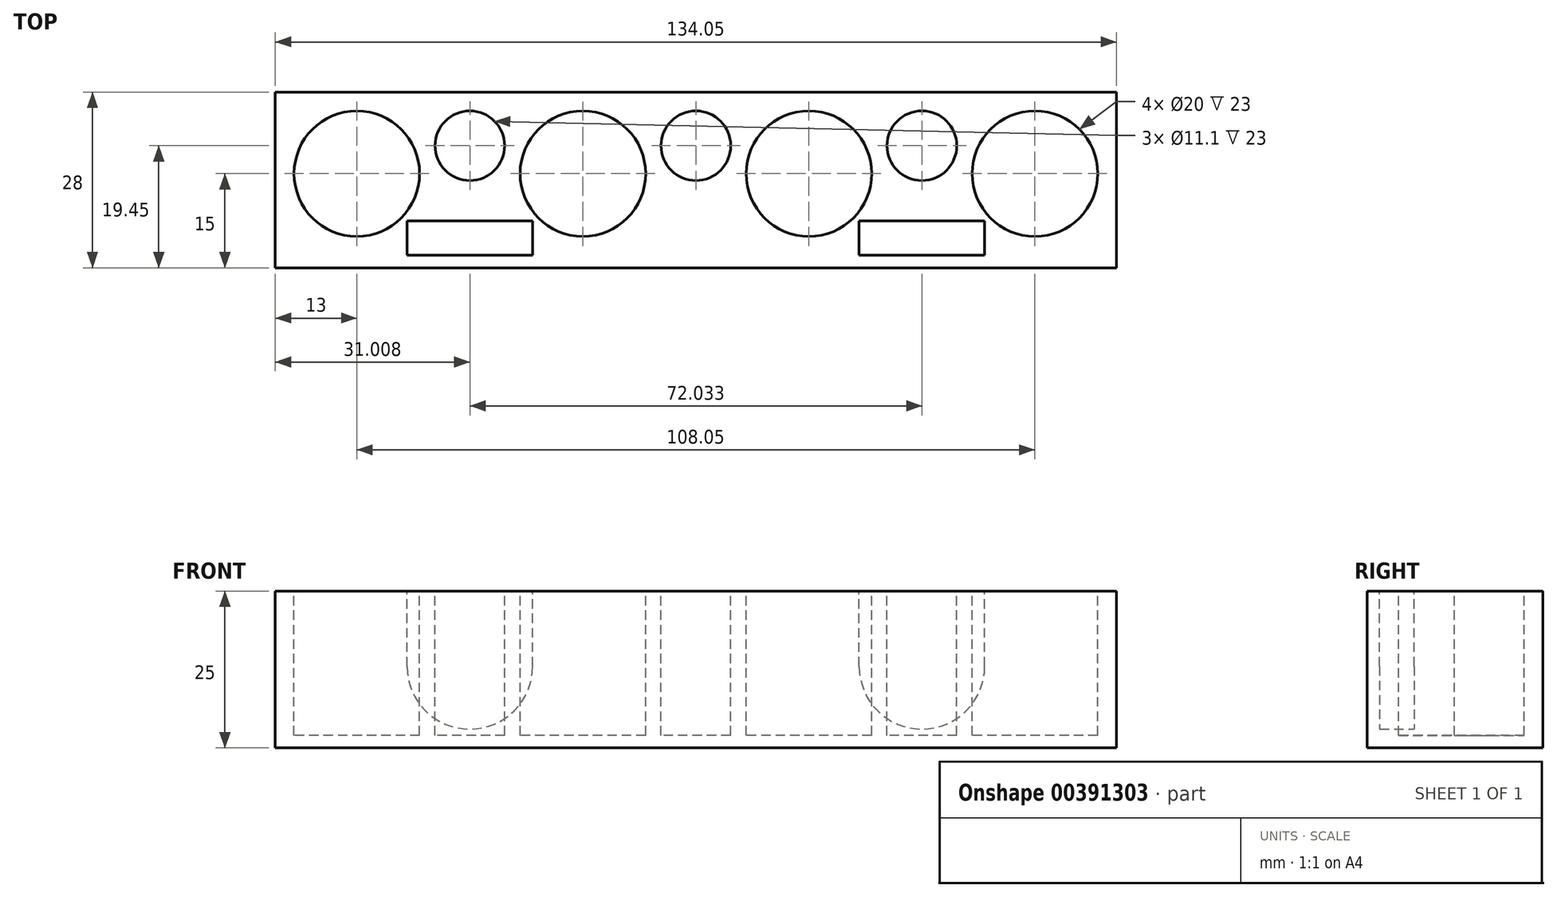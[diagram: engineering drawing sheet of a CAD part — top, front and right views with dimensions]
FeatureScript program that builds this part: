
annotation { "Feature Type Name" : "Feature", "Feature Type Description" : "" }
export const myFeature = defineFeature(function(context is Context, id is Id, definition is map)
    precondition{}
    {
        {
            var Q0;
            Q0=qCreatedBy(makeId("Top.planeOp"),FACE);
            var sketch = newSketch(context, id + "F0", { "sketchPlane" : qUnion([Q0])});
            skLineSegment(sketch, "E0.bottom", {"start": v(0, 0) * mm, "end": v(134.05, 0) * mm});
            skLineSegment(sketch, "E0.top", {"start": v(0, -28) * mm, "end": v(134.05, -28) * mm});
            skLineSegment(sketch, "E0.left", {"start": v(0, 0) * mm, "end": v(0, -28) * mm});
            skLineSegment(sketch, "E0.right", {"start": v(134.05, 0) * mm, "end": v(134.05, -28) * mm});
            skCircle(sketch, "E1", {"center": v(13, -13) * mm, "radius": 10 * mm});
            skCircle(sketch, "E2", {"center": v(31, -8.55) * mm, "radius": 5.55 * mm});
            skCircle(sketch, "E3", {"center": v(49.02, -13) * mm, "radius": 10 * mm});
            skCircle(sketch, "E4", {"center": v(67.02, -8.55) * mm, "radius": 5.55 * mm});
            skCircle(sketch, "E5", {"center": v(85.03, -13) * mm, "radius": 10 * mm});
            skCircle(sketch, "E6", {"center": v(103.04, -8.55) * mm, "radius": 5.55 * mm});
            skCircle(sketch, "E7", {"center": v(121.05, -13) * mm, "radius": 10 * mm});
            skLineSegment(sketch, "E8.bottom", {"start": v(21, -26) * mm, "end": v(41, -26) * mm});
            skLineSegment(sketch, "E8.top", {"start": v(21, -21) * mm, "end": v(41, -21) * mm});
            skLineSegment(sketch, "E8.left", {"start": v(21, -26) * mm, "end": v(21, -21) * mm});
            skLineSegment(sketch, "E8.right", {"start": v(41, -26) * mm, "end": v(41, -21) * mm});
            skCircle(sketch, "E9", {"center": v(31, -33.78) * mm, "radius": 17.5 * mm, "construction": true});
            skLineSegment(sketch, "E10", {"start": v(31, -33.78) * mm, "end": v(31, -13.78) * mm, "construction": true});
            skLineSegment(sketch, "E11", {"start": v(21, -23.5) * mm, "end": v(31, -23.5) * mm, "construction": true});
            skLineSegment(sketch, "E12", {"start": v(31, -23.5) * mm, "end": v(41, -23.78) * mm, "construction": true});
            skLineSegment(sketch, "E13.bottom", {"start": v(93.04, -26) * mm, "end": v(113.04, -26) * mm});
            skLineSegment(sketch, "E13.top", {"start": v(93.04, -21) * mm, "end": v(113.04, -21) * mm});
            skLineSegment(sketch, "E13.left", {"start": v(93.04, -26) * mm, "end": v(93.04, -21) * mm});
            skLineSegment(sketch, "E13.right", {"start": v(113.04, -26) * mm, "end": v(113.04, -21) * mm});
            skCircle(sketch, "E14", {"center": v(103.04, -33.78) * mm, "radius": 17.5 * mm, "construction": true});
            skLineSegment(sketch, "E15", {"start": v(103.04, -33.78) * mm, "end": v(103.04, -13.78) * mm, "construction": true});
            skLineSegment(sketch, "E16", {"start": v(103.04, -23.78) * mm, "end": v(93.04, -23.78) * mm, "construction": true});
            skLineSegment(sketch, "E17", {"start": v(103.04, -23.78) * mm, "end": v(113.04, -23.78) * mm, "construction": true});
            skSolve(sketch);
        }
        {
            var Q0;
            Q0=makeQuery(id+"F0.imprint","IMPRINT",FACE,{"disambiguationData":[TD([[makeQuery(id+"F0.imprint","IMPRINT",EDGE,{"derivedFrom":sQuery(id+"F0.wireOp",EDGE,"E0.bottom")}),-1.0]])]});
            var Q1;
            Q1=makeQuery(id+"F0.imprint","IMPRINT",FACE,{"disambiguationData":[TD([[makeQuery(id+"F0.imprint","IMPRINT",EDGE,{"derivedFrom":sQuery(id+"F0.wireOp",EDGE,"E8.bottom")}),1.0]])]});
            var Q2;
            Q2=makeQuery(id+"F0.imprint","IMPRINT",FACE,{"disambiguationData":[TD([[makeQuery(id+"F0.imprint","IMPRINT",EDGE,{"derivedFrom":sQuery(id+"F0.wireOp",EDGE,"E13.bottom")}),1.0]])]});
            extrude(context, id + "F1", {"entities" : qUnion([Q0, Q1, Q2]), "oppositeDirection" : true, "depth" : 23 * mm});
        }
        {
            var Q0;
            Q0=qCreatedBy(makeId("Front.planeOp"),FACE);
            var sketch = newSketch(context, id + "F2", { "sketchPlane" : qUnion([Q0])});
            skCircle(sketch, "E18", {"center": v(31, -12) * mm, "radius": 10 * mm});
            skLineSegment(sketch, "E19", {"start": v(0, 0) * mm, "end": v(0, -140.9) * mm, "construction": true});
            skCircle(sketch, "E20", {"center": v(103.04, -12) * mm, "radius": 10 * mm});
            skLineSegment(sketch, "E21.bottom", {"start": v(21, -12) * mm, "end": v(41, -12) * mm});
            skLineSegment(sketch, "E21.top", {"start": v(21, 6) * mm, "end": v(41, 6) * mm});
            skLineSegment(sketch, "E21.left", {"start": v(21, -12) * mm, "end": v(21, 6) * mm});
            skLineSegment(sketch, "E21.right", {"start": v(41, -12) * mm, "end": v(41, 6) * mm});
            skLineSegment(sketch, "E22.bottom", {"start": v(93.04, -12) * mm, "end": v(113.04, -12) * mm});
            skLineSegment(sketch, "E22.top", {"start": v(93.04, 6) * mm, "end": v(113.04, 6) * mm});
            skLineSegment(sketch, "E22.left", {"start": v(93.04, -12) * mm, "end": v(93.04, 6) * mm});
            skLineSegment(sketch, "E22.right", {"start": v(113.04, -12) * mm, "end": v(113.04, 6) * mm});
            skSolve(sketch);
        }
        {
            var Q0;
            Q0 = qSketchRegion(id + "F2", true);
            extrude(context, id + "F3", {"entities" : qUnion([Q0]), "operationType" : NewBodyOperationType.REMOVE, "depth" : 26 * mm, "hasSecondDirection" : true, "secondDirectionOppositeDirection" : false, "secondDirectionDepth" : 20.5 * mm});
        }
        {
            var Q0;
            Q0=qCreatedBy(makeId("Front.planeOp"),FACE);
            var sketch = newSketch(context, id + "F4", { "sketchPlane" : qUnion([Q0])});
            skLineSegment(sketch, "E23.bottom", {"start": v(0, -25) * mm, "end": v(134.05, -25) * mm});
            skLineSegment(sketch, "E23.top", {"start": v(0, -23) * mm, "end": v(134.05, -23) * mm});
            skLineSegment(sketch, "E23.left", {"start": v(0, -25) * mm, "end": v(0, -23) * mm});
            skLineSegment(sketch, "E23.right", {"start": v(134.05, -25) * mm, "end": v(134.05, -23) * mm});
            skSolve(sketch);
        }
        {
            var Q0;
            Q0 = qSketchRegion(id + "F4", true);
            var Q1;
            Q1=sQuery(id+"F4.wireOp",EDGE,"E23.bottom");
            var Q2;
            Q2=sQuery(id+"F4.wireOp",EDGE,"E23.top");
            var Q3;
            Q3=sQuery(id+"F4.wireOp",EDGE,"E23.right");
            var Q4;
            Q4=sQuery(id+"F4.wireOp",EDGE,"E23.left");
            extrude(context, id + "F5", {"entities" : qUnion([Q0]), "operationType" : NewBodyOperationType.ADD, "surfaceEntities" : qUnion([Q1, Q2, Q3, Q4]), "depth" : 28 * mm});
        }
    });
